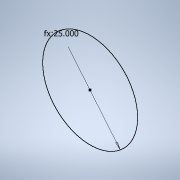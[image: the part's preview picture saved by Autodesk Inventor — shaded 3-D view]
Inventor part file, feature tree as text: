
AUTODESK INVENTOR PART (.ipt)
format: ipt  version: 2020 (Build 240168000, 168)  size: 84,992 bytes
history: native  units: in
note: dims shown in document units (in); Inventor stores cm internally (conversion verified against a paired STEP export)
features: sketch x1
ambient origin geometry x8: Origin, YZ Plane, XZ Plane, XY Plane, X Axis, Y Axis, Z Axis, Center Point
feature tree (1):
  sketch  "Sketch1"  dims[d0=25.0in]
